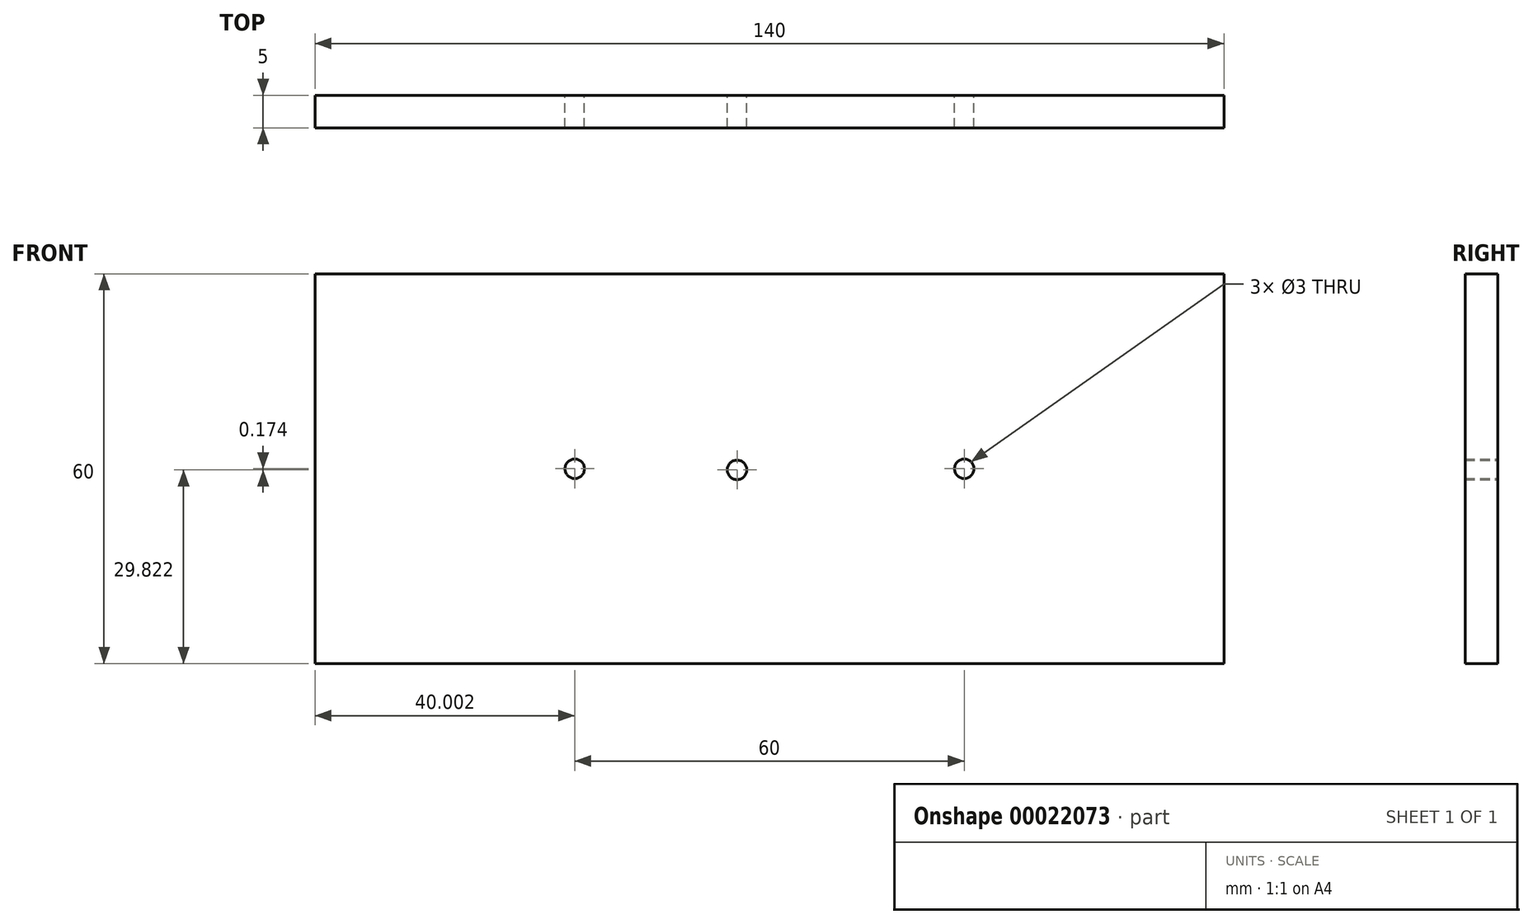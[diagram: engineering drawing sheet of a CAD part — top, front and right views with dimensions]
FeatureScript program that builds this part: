
annotation { "Feature Type Name" : "Feature", "Feature Type Description" : "" }
export const myFeature = defineFeature(function(context is Context, id is Id, definition is map)
    precondition{}
    {
        {
            var Q0;
            Q0=qCreatedBy(makeId("Front.planeOp"),FACE);
            var sketch = newSketch(context, id + "F0", { "sketchPlane" : qUnion([Q0])});
            skCircle(sketch, "E0", {"center": v(9.7, -14.34) * mm, "radius": 1.5 * mm});
            skCircle(sketch, "E1", {"center": v(69.7, -14.34) * mm, "radius": 1.5 * mm});
            skLineSegment(sketch, "E2", {"start": v(-30.3, 15.66) * mm, "end": v(-30.3, -44.34) * mm});
            skLineSegment(sketch, "E3", {"start": v(-30.3, -44.34) * mm, "end": v(109.7, -44.34) * mm});
            skLineSegment(sketch, "E4", {"start": v(-30.3, 15.66) * mm, "end": v(109.7, 15.66) * mm});
            skLineSegment(sketch, "E5", {"start": v(109.7, -44.34) * mm, "end": v(109.7, 15.66) * mm});
            skCircle(sketch, "E6", {"center": v(34.7, -14.52) * mm, "radius": 1.5 * mm});
            skSolve(sketch);
        }
        {
            var Q0;
            Q0 = qSketchRegion(id + "F0", true);
            extrude(context, id + "F1", {"entities" : qUnion([Q0]), "endBound" : BoundingType.SYMMETRIC, "depth" : 5 * mm});
        }
    });
